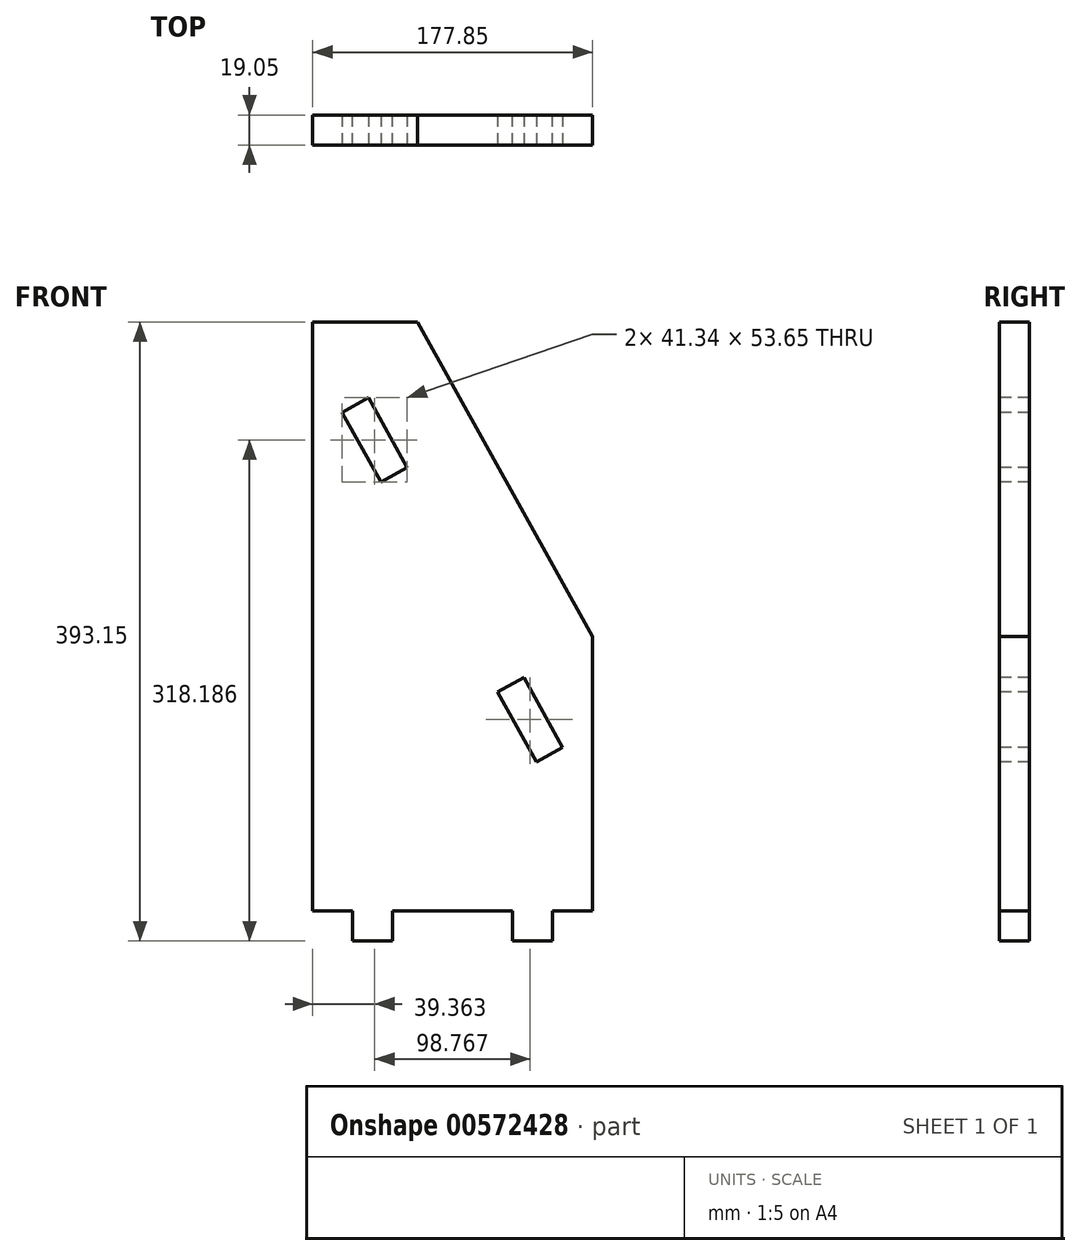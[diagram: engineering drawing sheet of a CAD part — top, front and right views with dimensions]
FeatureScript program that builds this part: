
annotation { "Feature Type Name" : "Feature", "Feature Type Description" : "" }
export const myFeature = defineFeature(function(context is Context, id is Id, definition is map)
    precondition{}
    {
        {
            var Q0;
            Q0=qCreatedBy(makeId("Front.planeOp"),FACE);
            var sketch = newSketch(context, id + "F0", { "sketchPlane" : qUnion([Q0])});
            skLineSegment(sketch, "E0", {"start": v(-17.78, 189.6) * mm, "end": v(-84.48, 189.6) * mm});
            skLineSegment(sketch, "E1", {"start": v(-84.48, 189.6) * mm, "end": v(-84.48, -184.49) * mm});
            skLineSegment(sketch, "E2", {"start": v(-84.48, -184.49) * mm, "end": v(93.37, -184.49) * mm});
            skLineSegment(sketch, "E3", {"start": v(93.37, -184.49) * mm, "end": v(93.37, -10.24) * mm});
            skLineSegment(sketch, "E4", {"start": v(-17.78, 189.6) * mm, "end": v(93.37, -10.24) * mm});
            skLineSegment(sketch, "E5", {"start": v(67.97, -184.49) * mm, "end": v(67.97, -203.54) * mm});
            skLineSegment(sketch, "E6", {"start": v(67.97, -203.54) * mm, "end": v(42.57, -203.54) * mm});
            skLineSegment(sketch, "E7", {"start": v(42.57, -203.54) * mm, "end": v(42.57, -184.49) * mm});
            skLineSegment(sketch, "E8", {"start": v(-33.68, -184.49) * mm, "end": v(-33.68, -203.54) * mm});
            skLineSegment(sketch, "E9", {"start": v(-33.68, -203.54) * mm, "end": v(-59.08, -203.54) * mm});
            skLineSegment(sketch, "E10", {"start": v(-59.08, -203.54) * mm, "end": v(-59.08, -184.49) * mm});
            skSolve(sketch);
        }
        {
            var Q0;
            Q0=makeQuery(id+"F0.imprint","IMPRINT",FACE,{"disambiguationData":[TD([[makeQuery(id+"F0.imprint","IMPRINT",EDGE,{"derivedFrom":sQuery(id+"F0.wireOp",EDGE,"E0")}),1.0]])]});
            var Q1;
            {var subQ0=sQuery(id+"F0.wireOp",EDGE,"E5");Q1=makeQuery(id+"F0.imprint","IMPRINT",FACE,{"disambiguationData":[TD([[makeQuery(id+"F0.imprint","IMPRINT",EDGE,{"derivedFrom":subQ0}),-1.0]])]});}
            var Q2;
            {var subQ0=sQuery(id+"F0.wireOp",EDGE,"E8");Q2=makeQuery(id+"F0.imprint","IMPRINT",FACE,{"disambiguationData":[TD([[makeQuery(id+"F0.imprint","IMPRINT",EDGE,{"derivedFrom":subQ0}),-1.0]])]});}
            extrude(context, id + "F1", {"entities" : qUnion([Q0, Q1, Q2]), "depth" : 19.05 * mm, "offsetDistance" : 25.4 * mm});
        }
        {
            var Q0;
            Q0=makeQuery(id+"F1.opExtrude","CAP_FACE",FACE,{"disambiguationData":[OSD([sQuery(id+"F0.wireOp",EDGE,"E0"),sQuery(id+"F0.wireOp",EDGE,"E1"),sQuery(id+"F0.wireOp",EDGE,"E2"),sQuery(id+"F0.wireOp",EDGE,"E3"),sQuery(id+"F0.wireOp",EDGE,"E4"),sQuery(id+"F0.wireOp",EDGE,"E5"),sQuery(id+"F0.wireOp",EDGE,"E6"),sQuery(id+"F0.wireOp",EDGE,"E7"),sQuery(id+"F0.wireOp",EDGE,"E8"),sQuery(id+"F0.wireOp",EDGE,"E9"),sQuery(id+"F0.wireOp",EDGE,"E10")])],"isStart":false});
            var sketch = newSketch(context, id + "F2", { "sketchPlane" : qUnion([Q0])});
            skLineSegment(sketch, "E11.0", {"start": v(-17.78, 189.6) * mm, "end": v(93.37, -10.24) * mm});
            skLineSegment(sketch, "E12.0", {"start": v(-49.14, 141.47) * mm, "end": v(-24.45, 97.08) * mm});
            skLineSegment(sketch, "E13.0", {"start": v(-65.79, 132.21) * mm, "end": v(-41.1, 87.82) * mm});
            skLineSegment(sketch, "E14", {"start": v(-65.79, 132.21) * mm, "end": v(-49.14, 141.47) * mm});
            skLineSegment(sketch, "E15.0", {"start": v(-41.1, 87.82) * mm, "end": v(-24.45, 97.08) * mm});
            skLineSegment(sketch, "E16.0", {"start": v(32.98, -45.37) * mm, "end": v(49.63, -36.1) * mm});
            skLineSegment(sketch, "E17.trimOffspring", {"start": v(32.98, -45.37) * mm, "end": v(57.67, -89.76) * mm});
            skLineSegment(sketch, "E18.trimOffspring", {"start": v(49.63, -36.1) * mm, "end": v(74.32, -80.5) * mm});
            skLineSegment(sketch, "E19.0", {"start": v(74.32, -184.49) * mm, "end": v(74.32, -10.24) * mm, "construction": true});
            skLineSegment(sketch, "E20", {"start": v(74.32, -80.5) * mm, "end": v(57.67, -89.76) * mm});
            skLineSegment(sketch, "E21", {"start": v(93.37, -114.76) * mm, "end": v(-75.9, 189.6) * mm, "construction": true});
            skLineSegment(sketch, "E22.0", {"start": v(93.37, -184.49) * mm, "end": v(93.37, -10.24) * mm});
            skLineSegment(sketch, "E23.0", {"start": v(-17.78, 189.6) * mm, "end": v(-84.48, 189.6) * mm});
            skSolve(sketch);
        }
        {
            var Q0;
            Q0 = qSketchRegion(id + "F2", true);
            extrude(context, id + "F3", {"entities" : qUnion([Q0]), "operationType" : NewBodyOperationType.REMOVE, "endBound" : BoundingType.THROUGH_ALL, "oppositeDirection" : true, "depth" : 25.4 * mm, "offsetDistance" : 25.4 * mm});
        }
    });
